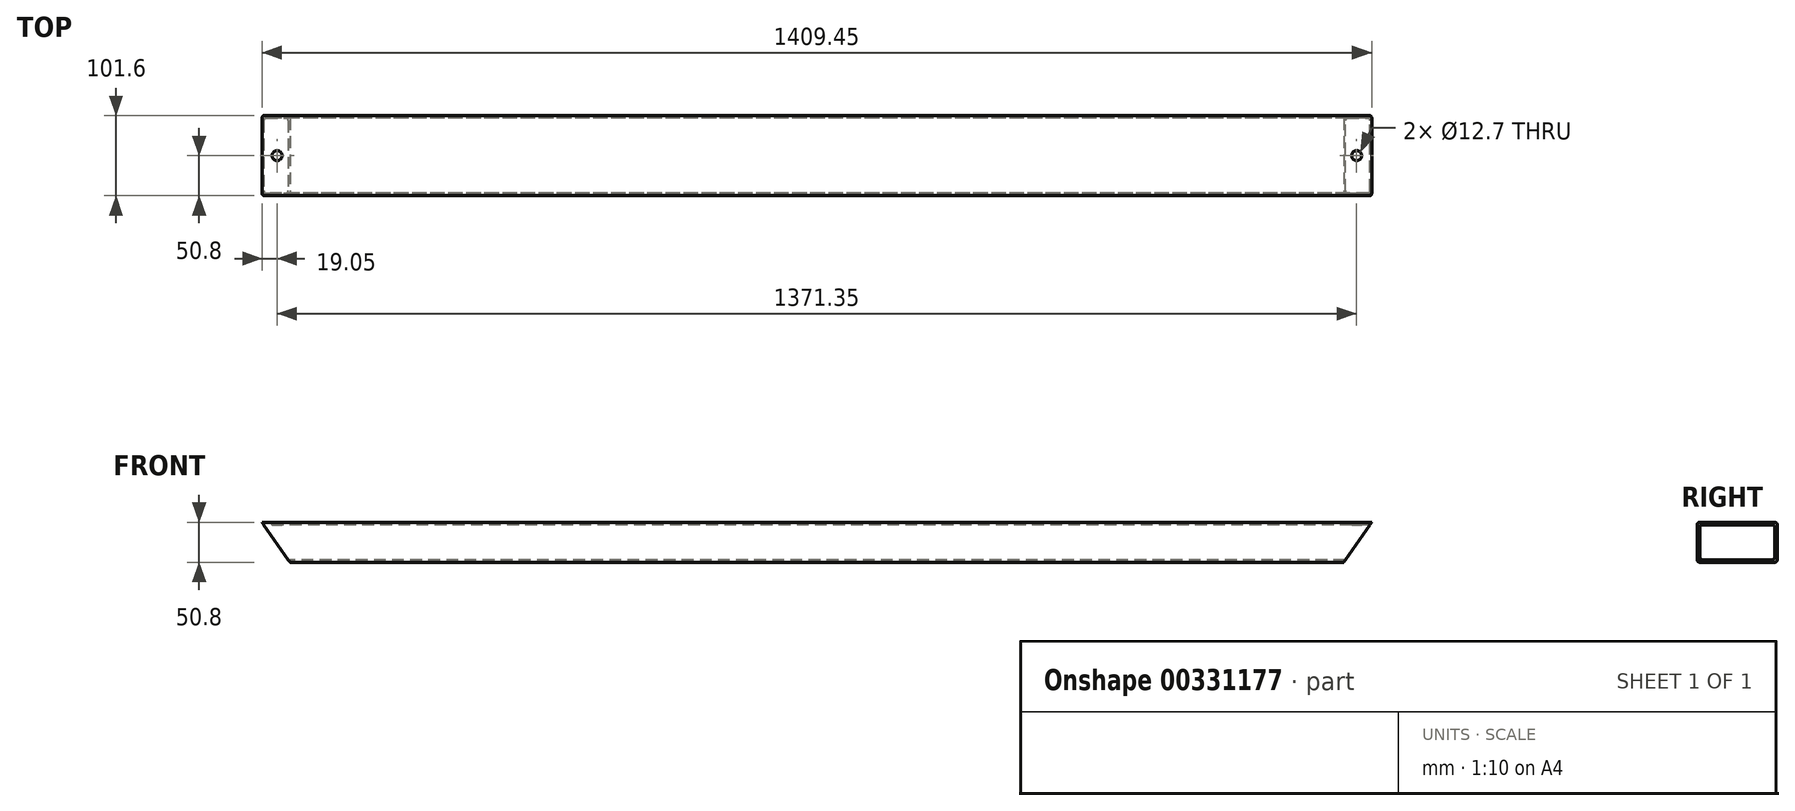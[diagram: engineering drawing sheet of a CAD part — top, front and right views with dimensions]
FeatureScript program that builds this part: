
annotation { "Feature Type Name" : "Feature", "Feature Type Description" : "" }
export const myFeature = defineFeature(function(context is Context, id is Id, definition is map)
    precondition{}
    {
        {
            var Q0;
            Q0=qCreatedBy(makeId("Right.planeOp"),FACE);
            var sketch = newSketch(context, id + "F0", { "sketchPlane" : qUnion([Q0])});
            skLineSegment(sketch, "E0.bottom", {"start": v(47.63, -25.4) * mm, "end": v(-47.62, -25.4) * mm});
            skLineSegment(sketch, "E0.top", {"start": v(47.62, 25.4) * mm, "end": v(-47.63, 25.4) * mm});
            skLineSegment(sketch, "E0.left", {"start": v(50.8, -22.22) * mm, "end": v(50.8, 22.23) * mm});
            skLineSegment(sketch, "E0.right", {"start": v(-50.8, -22.23) * mm, "end": v(-50.8, 22.22) * mm});
            skPoint(sketch, "E0.middle", {"position": v(0, 0) * mm});
            skLineSegment(sketch, "E1.bottom", {"start": v(44.45, 22.23) * mm, "end": v(-44.45, 22.22) * mm});
            skLineSegment(sketch, "E1.top", {"start": v(44.45, -22.22) * mm, "end": v(-44.45, -22.23) * mm});
            skLineSegment(sketch, "E1.left", {"start": v(47.62, 19.05) * mm, "end": v(47.63, -19.05) * mm});
            skLineSegment(sketch, "E1.right", {"start": v(-47.63, 19.05) * mm, "end": v(-47.62, -19.05) * mm});
            skPoint(sketch, "E2.visualSharp", {"position": v(-47.63, 22.22) * mm});
            skArc(sketch, "E2.filletArc", {"start": v(-44.45, 22.22) * mm, "mid": v(-46.7, 21.3) * mm, "end": v(-47.63, 19.05) * mm});
            skPoint(sketch, "E3.visualSharp", {"position": v(-50.8, 25.4) * mm});
            skArc(sketch, "E3.filletArc", {"start": v(-47.63, 25.4) * mm, "mid": v(-49.87, 24.47) * mm, "end": v(-50.8, 22.22) * mm});
            skPoint(sketch, "E4.visualSharp", {"position": v(-47.62, -22.23) * mm});
            skArc(sketch, "E4.filletArc", {"start": v(-47.62, -19.05) * mm, "mid": v(-46.7, -21.3) * mm, "end": v(-44.45, -22.23) * mm});
            skPoint(sketch, "E5.visualSharp", {"position": v(-50.8, -25.4) * mm});
            skArc(sketch, "E5.filletArc", {"start": v(-50.8, -22.23) * mm, "mid": v(-49.87, -24.47) * mm, "end": v(-47.62, -25.4) * mm});
            skPoint(sketch, "E6.visualSharp", {"position": v(47.62, 22.23) * mm});
            skArc(sketch, "E6.filletArc", {"start": v(47.62, 19.05) * mm, "mid": v(46.7, 21.3) * mm, "end": v(44.45, 22.23) * mm});
            skPoint(sketch, "E7.visualSharp", {"position": v(47.63, -22.22) * mm});
            skArc(sketch, "E7.filletArc", {"start": v(44.45, -22.22) * mm, "mid": v(46.7, -21.3) * mm, "end": v(47.63, -19.05) * mm});
            skPoint(sketch, "E8.visualSharp", {"position": v(50.8, -25.4) * mm});
            skArc(sketch, "E8.filletArc", {"start": v(47.63, -25.4) * mm, "mid": v(49.87, -24.47) * mm, "end": v(50.8, -22.22) * mm});
            skPoint(sketch, "E9.visualSharp", {"position": v(50.8, 25.4) * mm});
            skArc(sketch, "E9.filletArc", {"start": v(50.8, 22.23) * mm, "mid": v(49.87, 24.47) * mm, "end": v(47.62, 25.4) * mm});
            skSolve(sketch);
        }
        {
            var Q0;
            Q0 = qSketchRegion(id + "F0", true);
            extrude(context, id + "F1", {"entities" : qUnion([Q0]), "depth" : 1409.45 * mm});
        }
        {
            var Q0;
            Q0=qCreatedBy(makeId("Front.planeOp"),FACE);
            var sketch = newSketch(context, id + "F2", { "sketchPlane" : qUnion([Q0])});
            skLineSegment(sketch, "E10", {"start": v(0, -25.4) * mm, "end": v(35.57, -25.4) * mm});
            skLineSegment(sketch, "E11", {"start": v(35.57, -25.4) * mm, "end": v(0, 25.4) * mm});
            skLineSegment(sketch, "E12", {"start": v(0, 25.4) * mm, "end": v(0, -25.4) * mm});
            skLineSegment(sketch, "E13", {"start": v(1373.88, -25.4) * mm, "end": v(1409.45, -25.4) * mm});
            skLineSegment(sketch, "E14", {"start": v(1409.45, -25.4) * mm, "end": v(1409.45, 25.4) * mm});
            skLineSegment(sketch, "E15", {"start": v(1409.45, 25.4) * mm, "end": v(1373.88, -25.4) * mm});
            skSolve(sketch);
        }
        {
            var Q0;
            Q0 = qSketchRegion(id + "F2", true);
            extrude(context, id + "F3", {"entities" : qUnion([Q0]), "operationType" : NewBodyOperationType.REMOVE, "endBound" : BoundingType.THROUGH_ALL, "oppositeDirection" : true, "depth" : 25.4 * mm, "hasSecondDirection" : true, "secondDirectionBound" : SecondDirectionBoundingType.THROUGH_ALL, "secondDirectionOppositeDirection" : false, "secondDirectionDepth" : 25.4 * mm});
        }
        {
            var Q0;
            Q0=makeQuery(id+"F1.opExtrude","SWEPT_FACE",FACE,{"disambiguationData":[OSD([sQuery(id+"F0.wireOp",EDGE,"E0.top")])]});
            var sketch = newSketch(context, id + "F4", { "sketchPlane" : qUnion([Q0])});
            skCircle(sketch, "E16", {"center": v(19.05, 0) * mm, "radius": 6.35 * mm});
            skCircle(sketch, "E17", {"center": v(1390.4, 0) * mm, "radius": 6.35 * mm});
            skPoint(sketch, "E17.centerSnap0", {"position": v(1409.45, 0) * mm});
            skSolve(sketch);
        }
        {
            var Q0;
            Q0 = qSketchRegion(id + "F4", true);
            extrude(context, id + "F5", {"entities" : qUnion([Q0]), "operationType" : NewBodyOperationType.REMOVE, "oppositeDirection" : true, "depth" : 25.4 * mm});
        }
    });
